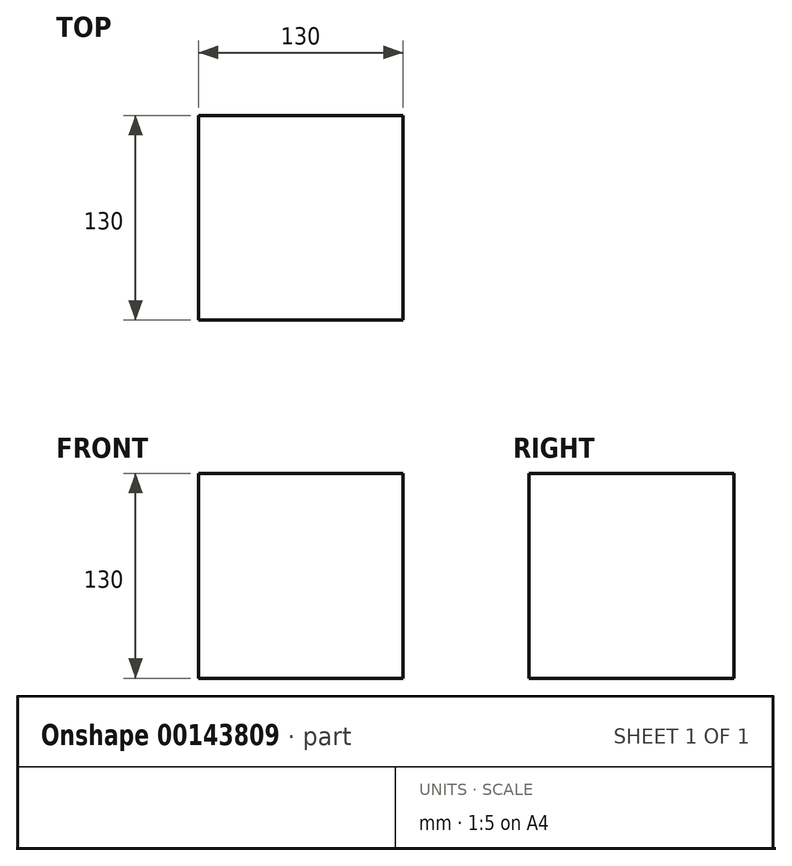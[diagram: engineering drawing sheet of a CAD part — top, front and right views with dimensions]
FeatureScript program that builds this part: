
annotation { "Feature Type Name" : "Feature", "Feature Type Description" : "" }
export const myFeature = defineFeature(function(context is Context, id is Id, definition is map)
    precondition{}
    {
        {
            var Q0;
            Q0=qCreatedBy(makeId("Top.planeOp"),FACE);
            var sketch = newSketch(context, id + "F0", { "sketchPlane" : qUnion([Q0])});
            skLineSegment(sketch, "E0.bottom", {"start": v(-49.4, -96.44) * mm, "end": v(80.6, -96.44) * mm});
            skLineSegment(sketch, "E0.top", {"start": v(-49.4, 33.56) * mm, "end": v(80.6, 33.56) * mm});
            skLineSegment(sketch, "E0.left", {"start": v(-49.4, -96.44) * mm, "end": v(-49.4, 33.56) * mm});
            skLineSegment(sketch, "E0.right", {"start": v(80.6, -96.44) * mm, "end": v(80.6, 33.56) * mm});
            skSolve(sketch);
        }
        {
            var Q0;
            Q0 = qSketchRegion(id + "F0", true);
            extrude(context, id + "F1", {"entities" : qUnion([Q0]), "depth" : 130 * mm});
        }
    });
